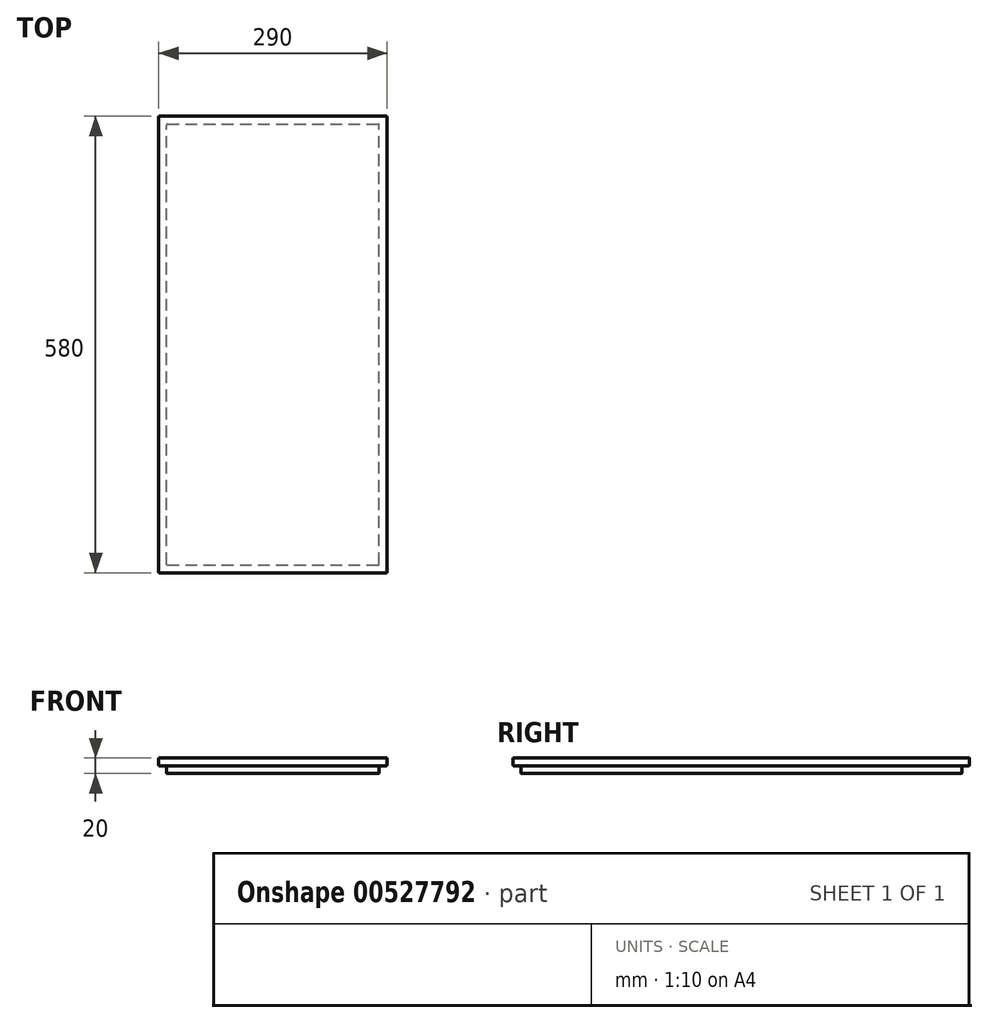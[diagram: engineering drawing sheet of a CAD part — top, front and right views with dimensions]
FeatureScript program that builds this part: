
annotation { "Feature Type Name" : "Feature", "Feature Type Description" : "" }
export const myFeature = defineFeature(function(context is Context, id is Id, definition is map)
    precondition{}
    {
        {
            var Q0;
            Q0=qCreatedBy(makeId("Top.planeOp"),FACE);
            var sketch = newSketch(context, id + "F0", { "sketchPlane" : qUnion([Q0])});
            skLineSegment(sketch, "E0.bottom", {"start": v(-184.62, -285.51) * mm, "end": v(105.38, -285.51) * mm});
            skLineSegment(sketch, "E0.top", {"start": v(-184.62, 294.49) * mm, "end": v(105.38, 294.49) * mm});
            skLineSegment(sketch, "E0.left", {"start": v(-184.62, -285.51) * mm, "end": v(-184.62, 294.49) * mm});
            skLineSegment(sketch, "E0.right", {"start": v(105.38, -285.51) * mm, "end": v(105.38, 294.49) * mm});
            skSolve(sketch);
        }
        {
            var Q0;
            Q0 = qSketchRegion(id + "F0", true);
            extrude(context, id + "F1", {"entities" : qUnion([Q0]), "depth" : 10 * mm, "offsetDistance" : 25 * mm});
        }
        {
            var Q0;
            Q0=makeQuery(id+"F1.opExtrude","CAP_FACE",FACE,{"disambiguationData":[OSD([sQuery(id+"F0.wireOp",EDGE,"E0.bottom"),sQuery(id+"F0.wireOp",EDGE,"E0.top"),sQuery(id+"F0.wireOp",EDGE,"E0.left"),sQuery(id+"F0.wireOp",EDGE,"E0.right")])],"isStart":true});
            var sketch = newSketch(context, id + "F2", { "sketchPlane" : qUnion([Q0])});
            skLineSegment(sketch, "E1.bottom", {"start": v(-174.62, 275.51) * mm, "end": v(95.38, 275.51) * mm});
            skLineSegment(sketch, "E1.top", {"start": v(-174.62, -284.49) * mm, "end": v(95.38, -284.49) * mm});
            skLineSegment(sketch, "E1.left", {"start": v(-174.62, 275.51) * mm, "end": v(-174.62, -284.49) * mm});
            skLineSegment(sketch, "E1.right", {"start": v(95.38, 275.51) * mm, "end": v(95.38, -284.49) * mm});
            skSolve(sketch);
        }
        {
            var Q0;
            Q0=makeQuery(id+"F2.imprint","IMPRINT",FACE,{"disambiguationData":[TD([[makeQuery(id+"F2.imprint","IMPRINT",EDGE,{"derivedFrom":sQuery(id+"F2.wireOp",EDGE,"E1.bottom")}),-1.0]])]});
            extrude(context, id + "F3", {"entities" : qUnion([Q0]), "operationType" : NewBodyOperationType.ADD, "depth" : 10 * mm, "offsetDistance" : 25 * mm});
        }
        {
            var Q0;
            Q0=makeQuery(id+"F3.opExtrude","CAP_FACE",FACE,{"disambiguationData":[OSD([sQuery(id+"F2.wireOp",EDGE,"E1.bottom"),sQuery(id+"F2.wireOp",EDGE,"E1.top"),sQuery(id+"F2.wireOp",EDGE,"E1.left"),sQuery(id+"F2.wireOp",EDGE,"E1.right")])],"isStart":false});
            var Q1;
            Q1=makeQuery(id+"F1.opExtrude","CAP_EDGE",EDGE,{"disambiguationData":[OSD([sQuery(id+"F0.wireOp",EDGE,"E0.left")])],"isStart":true});
            var Q2;
            Q2=makeQuery(id+"F3.opExtrude","SWEPT_FACE",FACE,{"disambiguationData":[OSD([sQuery(id+"F2.wireOp",EDGE,"E1.bottom")])]});
            var Q3;
            Q3=makeQuery(id+"F3.opExtrude","SWEPT_FACE",FACE,{"disambiguationData":[OSD([sQuery(id+"F2.wireOp",EDGE,"E1.right")])]});
            var Q4;
            Q4=makeQuery(id+"F1.opExtrude","SWEPT_FACE",FACE,{"disambiguationData":[OSD([sQuery(id+"F0.wireOp",EDGE,"E0.right")])]});
            var Q5;
            Q5=makeQuery(id+"F1.opExtrude","SWEPT_FACE",FACE,{"disambiguationData":[OSD([sQuery(id+"F0.wireOp",EDGE,"E0.bottom")])]});
            var Q6;
            Q6=makeQuery(id+"F1.opExtrude","SWEPT_FACE",FACE,{"disambiguationData":[OSD([sQuery(id+"F0.wireOp",EDGE,"E0.left")])]});
            var Q7;
            Q7=makeQuery(id+"F1.opExtrude","SWEPT_FACE",FACE,{"disambiguationData":[OSD([sQuery(id+"F0.wireOp",EDGE,"E0.top")])]});
            var Q8;
            Q8=makeQuery(id+"F3.opExtrude","SWEPT_FACE",FACE,{"disambiguationData":[OSD([sQuery(id+"F2.wireOp",EDGE,"E1.top")])]});
            var Q9;
            Q9=makeQuery(id+"F3.opExtrude","SWEPT_FACE",FACE,{"disambiguationData":[OSD([sQuery(id+"F2.wireOp",EDGE,"E1.left")])]});
            fillet(context, id + "F4", {"entities" : qUnion([Q0, Q1, Q2, Q3, Q4, Q5, Q6, Q7, Q8, Q9]), "radius" : 1 * mm, "tangentPropagation" : true, "allowEdgeOverflow" : false});
        }
    });
